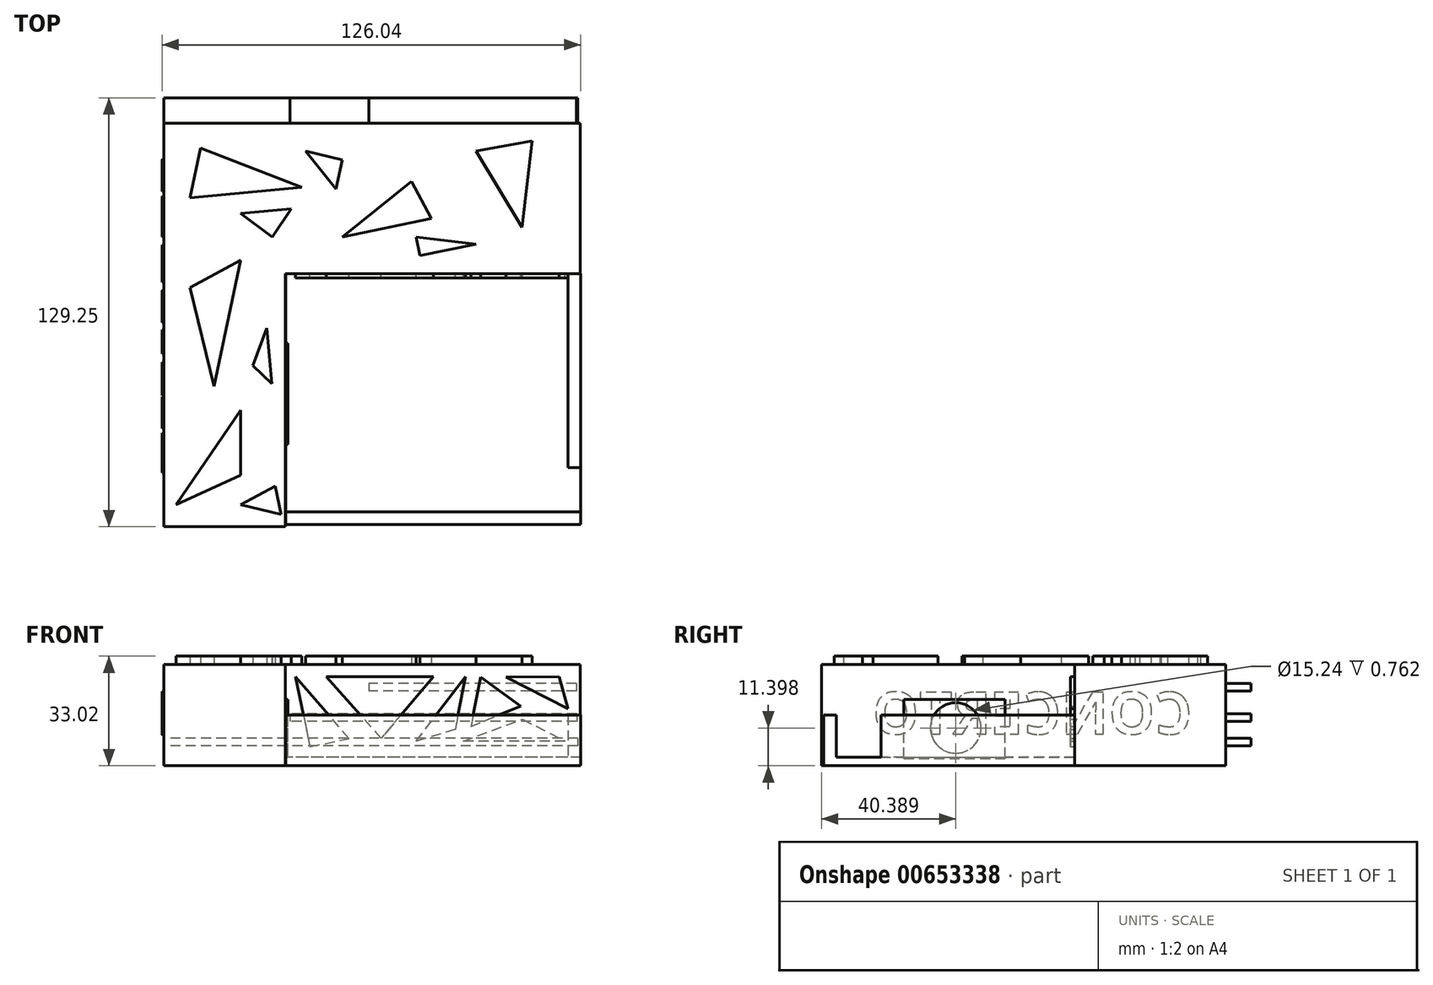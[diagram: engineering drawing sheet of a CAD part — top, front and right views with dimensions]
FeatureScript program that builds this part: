
annotation { "Feature Type Name" : "Feature", "Feature Type Description" : "" }
export const myFeature = defineFeature(function(context is Context, id is Id, definition is map)
    precondition{}
    {
        {
            var Q0;
            Q0=qCreatedBy(makeId("Top.planeOp"),FACE);
            var sketch = newSketch(context, id + "F0", { "sketchPlane" : qUnion([Q0])});
            skLineSegment(sketch, "E0.bottom", {"start": v(-61.74, 45.43) * mm, "end": v(63.6, 45.43) * mm});
            skLineSegment(sketch, "E0.top", {"start": v(-61.74, 0) * mm, "end": v(63.6, 0) * mm});
            skLineSegment(sketch, "E0.left", {"start": v(-61.74, 45.43) * mm, "end": v(-61.74, 0) * mm});
            skLineSegment(sketch, "E0.right", {"start": v(63.6, 45.43) * mm, "end": v(63.6, 0) * mm});
            skSolve(sketch);
        }
        {
            var Q0;
            Q0 = qSketchRegion(id + "F0", true);
            var Q1;
            Q1=makeQuery(id+"F0.imprint","IMPRINT",FACE,{"disambiguationData":[TD([[makeQuery(id+"F0.imprint","IMPRINT",EDGE,{"derivedFrom":sQuery(id+"F0.wireOp",EDGE,"E0.bottom")}),-1.0]])]});
            extrude(context, id + "F1", {"entities" : qUnion([Q0, Q1]), "depth" : 30.48 * mm, "offsetDistance" : 25.4 * mm});
        }
        {
            var Q0;
            Q0=makeQuery(id+"F1.opExtrude","SWEPT_FACE",FACE,{"disambiguationData":[OSD([sQuery(id+"F0.wireOp",EDGE,"E0.top")])]});
            var sketch = newSketch(context, id + "F2", { "sketchPlane" : qUnion([Q0])});
            skLineSegment(sketch, "E1.bottom", {"start": v(-61.74, 30.48) * mm, "end": v(-25.2, 30.48) * mm});
            skLineSegment(sketch, "E1.top", {"start": v(-61.74, 0) * mm, "end": v(-25.2, 0) * mm});
            skLineSegment(sketch, "E1.left", {"start": v(-61.74, 30.48) * mm, "end": v(-61.74, 0) * mm});
            skLineSegment(sketch, "E1.right", {"start": v(-25.2, 30.48) * mm, "end": v(-25.2, 0) * mm});
            skSolve(sketch);
        }
        {
            var Q0;
            Q0=makeQuery(id+"F2.imprint","IMPRINT",FACE,{"disambiguationData":[TD([[makeQuery(id+"F2.imprint","IMPRINT",EDGE,{"derivedFrom":sQuery(id+"F2.wireOp",EDGE,"E1.bottom")}),-1.0]])]});
            extrude(context, id + "F3", {"entities" : qUnion([Q0]), "operationType" : NewBodyOperationType.ADD, "depth" : 76.2 * mm, "offsetDistance" : 25.4 * mm});
        }
        {
            var Q0;
            Q0=qCreatedBy(makeId("Top.planeOp"),FACE);
            var sketch = newSketch(context, id + "F4", { "sketchPlane" : qUnion([Q0])});
            skLineSegment(sketch, "E2.bottom", {"start": v(63.8, 0) * mm, "end": v(-24.98, 0) * mm});
            skLineSegment(sketch, "E2.top", {"start": v(63.8, -75.57) * mm, "end": v(-24.98, -75.57) * mm});
            skLineSegment(sketch, "E2.left", {"start": v(63.8, 0) * mm, "end": v(63.8, -75.57) * mm});
            skLineSegment(sketch, "E2.right", {"start": v(-24.98, 0) * mm, "end": v(-24.98, -75.57) * mm});
            skSolve(sketch);
        }
        {
            var Q0;
            Q0=makeQuery(id+"F4.imprint","IMPRINT",FACE,{"disambiguationData":[TD([[makeQuery(id+"F4.imprint","IMPRINT",EDGE,{"derivedFrom":sQuery(id+"F4.wireOp",EDGE,"E2.bottom")}),1.0]])]});
            extrude(context, id + "F5", {"entities" : qUnion([Q0]), "operationType" : NewBodyOperationType.ADD, "depth" : 2.54 * mm, "offsetDistance" : 25.4 * mm});
        }
        {
            var Q0;
            Q0=makeQuery(id+"F3.boolean.opBoolean","MERGE",FACE,{"derivedFrom":[makeQuery(id+"F1.opExtrude","CAP_FACE",FACE,{"disambiguationData":[OSD([sQuery(id+"F0.wireOp",EDGE,"E0.bottom"),sQuery(id+"F0.wireOp",EDGE,"E0.top"),sQuery(id+"F0.wireOp",EDGE,"E0.left"),sQuery(id+"F0.wireOp",EDGE,"E0.right")])],"isStart":false}),makeQuery(id+"F3.opExtrude","SWEPT_FACE",FACE,{"disambiguationData":[OSD([sQuery(id+"F2.wireOp",EDGE,"E1.bottom")])]})]});
            var sketch = newSketch(context, id + "F6", { "sketchPlane" : qUnion([Q0])});
            skLineSegment(sketch, "E3", {"start": v(-58.02, -69.58) * mm, "end": v(-38.61, -41.09) * mm});
            skLineSegment(sketch, "E4", {"start": v(-38.61, -41.09) * mm, "end": v(-38.61, -60.7) * mm});
            skLineSegment(sketch, "E5", {"start": v(-38.61, -60.7) * mm, "end": v(-58.02, -69.58) * mm});
            skLineSegment(sketch, "E6", {"start": v(-53.9, -4.13) * mm, "end": v(-38.61, 4.13) * mm});
            skLineSegment(sketch, "E7", {"start": v(-38.61, 4.13) * mm, "end": v(-46.66, -33.86) * mm});
            skLineSegment(sketch, "E8", {"start": v(-46.66, -33.86) * mm, "end": v(-53.9, -4.13) * mm});
            skLineSegment(sketch, "E9", {"start": v(-53.9, 22.92) * mm, "end": v(-50.72, 37.86) * mm});
            skLineSegment(sketch, "E10", {"start": v(-50.72, 37.86) * mm, "end": v(-20.23, 26.02) * mm});
            skLineSegment(sketch, "E11", {"start": v(-20.23, 26.02) * mm, "end": v(-53.9, 22.92) * mm});
            skLineSegment(sketch, "E12", {"start": v(-8.05, 11.15) * mm, "end": v(12.8, 27.87) * mm});
            skLineSegment(sketch, "E13", {"start": v(12.8, 27.87) * mm, "end": v(18.85, 16.68) * mm});
            skLineSegment(sketch, "E14", {"start": v(18.85, 16.68) * mm, "end": v(-8.05, 11.15) * mm});
            skLineSegment(sketch, "E15", {"start": v(32.21, 36.96) * mm, "end": v(49.14, 40.06) * mm});
            skLineSegment(sketch, "E16", {"start": v(49.14, 40.06) * mm, "end": v(46.04, 14.04) * mm});
            skLineSegment(sketch, "E17", {"start": v(46.04, 14.04) * mm, "end": v(32.21, 36.96) * mm});
            skLineSegment(sketch, "E18", {"start": v(-38.61, 18.17) * mm, "end": v(-23.4, 19.57) * mm});
            skLineSegment(sketch, "E19", {"start": v(-23.4, 19.57) * mm, "end": v(-29.14, 11.15) * mm});
            skLineSegment(sketch, "E20", {"start": v(-29.14, 11.15) * mm, "end": v(-38.61, 18.17) * mm});
            skLineSegment(sketch, "E21", {"start": v(-34.9, -27.67) * mm, "end": v(-30.77, -16.31) * mm});
            skLineSegment(sketch, "E22", {"start": v(-30.77, -16.31) * mm, "end": v(-29.22, -33.12) * mm});
            skLineSegment(sketch, "E23", {"start": v(-29.22, -33.12) * mm, "end": v(-34.9, -27.67) * mm});
            skLineSegment(sketch, "E24", {"start": v(14.25, 11.15) * mm, "end": v(15.42, 5.45) * mm});
            skLineSegment(sketch, "E25", {"start": v(15.42, 5.45) * mm, "end": v(32.21, 8.9) * mm});
            skLineSegment(sketch, "E26", {"start": v(32.21, 8.9) * mm, "end": v(14.25, 11.15) * mm});
            skLineSegment(sketch, "E27", {"start": v(-19, 36.96) * mm, "end": v(-9.9, 25.61) * mm});
            skLineSegment(sketch, "E28", {"start": v(-9.9, 25.61) * mm, "end": v(-8.05, 34.32) * mm});
            skLineSegment(sketch, "E29", {"start": v(-8.05, 34.32) * mm, "end": v(-19, 36.96) * mm});
            skLineSegment(sketch, "E30", {"start": v(-38.61, -69.58) * mm, "end": v(-28.2, -63.95) * mm});
            skLineSegment(sketch, "E31", {"start": v(-28.2, -63.95) * mm, "end": v(-26.45, -72.43) * mm});
            skLineSegment(sketch, "E32", {"start": v(-26.45, -72.43) * mm, "end": v(-38.61, -69.58) * mm});
            skSolve(sketch);
        }
        {
            var Q0;
            Q0=makeQuery(id+"F6.imprint","IMPRINT",FACE,{"disambiguationData":[TD([[makeQuery(id+"F6.imprint","IMPRINT",EDGE,{"derivedFrom":sQuery(id+"F6.wireOp",EDGE,"E9")}),-1.0]])]});
            var Q1;
            Q1=makeQuery(id+"F6.imprint","IMPRINT",FACE,{"disambiguationData":[TD([[makeQuery(id+"F6.imprint","IMPRINT",EDGE,{"derivedFrom":sQuery(id+"F6.wireOp",EDGE,"E18")}),-1.0]])]});
            var Q2;
            Q2=makeQuery(id+"F6.imprint","IMPRINT",FACE,{"disambiguationData":[TD([[makeQuery(id+"F6.imprint","IMPRINT",EDGE,{"derivedFrom":sQuery(id+"F6.wireOp",EDGE,"E6")}),-1.0]])]});
            var Q3;
            Q3=makeQuery(id+"F6.imprint","IMPRINT",FACE,{"disambiguationData":[TD([[makeQuery(id+"F6.imprint","IMPRINT",EDGE,{"derivedFrom":sQuery(id+"F6.wireOp",EDGE,"E21")}),-1.0]])]});
            var Q4;
            Q4=makeQuery(id+"F6.imprint","IMPRINT",FACE,{"disambiguationData":[TD([[makeQuery(id+"F6.imprint","IMPRINT",EDGE,{"derivedFrom":sQuery(id+"F6.wireOp",EDGE,"E3")}),-1.0]])]});
            var Q5;
            Q5=makeQuery(id+"F6.imprint","IMPRINT",FACE,{"disambiguationData":[TD([[makeQuery(id+"F6.imprint","IMPRINT",EDGE,{"derivedFrom":sQuery(id+"F6.wireOp",EDGE,"E30")}),-1.0]])]});
            var Q6;
            Q6=makeQuery(id+"F6.imprint","IMPRINT",FACE,{"disambiguationData":[TD([[makeQuery(id+"F6.imprint","IMPRINT",EDGE,{"derivedFrom":sQuery(id+"F6.wireOp",EDGE,"E27")}),1.0]])]});
            var Q7;
            Q7=makeQuery(id+"F6.imprint","IMPRINT",FACE,{"disambiguationData":[TD([[makeQuery(id+"F6.imprint","IMPRINT",EDGE,{"derivedFrom":sQuery(id+"F6.wireOp",EDGE,"E12")}),-1.0]])]});
            var Q8;
            Q8=makeQuery(id+"F6.imprint","IMPRINT",FACE,{"disambiguationData":[TD([[makeQuery(id+"F6.imprint","IMPRINT",EDGE,{"derivedFrom":sQuery(id+"F6.wireOp",EDGE,"E24")}),1.0]])]});
            var Q9;
            Q9=makeQuery(id+"F6.imprint","IMPRINT",FACE,{"disambiguationData":[TD([[makeQuery(id+"F6.imprint","IMPRINT",EDGE,{"derivedFrom":sQuery(id+"F6.wireOp",EDGE,"E15")}),-1.0]])]});
            extrude(context, id + "F7", {"entities" : qUnion([Q0, Q1, Q2, Q3, Q4, Q5, Q6, Q7, Q8, Q9]), "operationType" : NewBodyOperationType.ADD, "depth" : 2.54 * mm, "offsetDistance" : 25.4 * mm});
        }
        {
            var Q0;
            Q0=makeQuery(id+"F1.opExtrude","SWEPT_FACE",FACE,{"disambiguationData":[OSD([sQuery(id+"F0.wireOp",EDGE,"E0.top")])]});
            var sketch = newSketch(context, id + "F8", { "sketchPlane" : qUnion([Q0])});
            skLineSegment(sketch, "E33", {"start": v(-22.1, 26.84) * mm, "end": v(-17.76, 5.78) * mm});
            skLineSegment(sketch, "E34", {"start": v(-17.76, 5.78) * mm, "end": v(-6.02, 8.2) * mm});
            skLineSegment(sketch, "E35", {"start": v(-6.02, 8.2) * mm, "end": v(-22.1, 26.84) * mm});
            skLineSegment(sketch, "E36", {"start": v(-12.8, 26.84) * mm, "end": v(19.4, 26.84) * mm});
            skLineSegment(sketch, "E37", {"start": v(19.4, 26.84) * mm, "end": v(3.72, 8.26) * mm});
            skLineSegment(sketch, "E38", {"start": v(3.72, 8.26) * mm, "end": v(-12.8, 26.84) * mm});
            skLineSegment(sketch, "E39", {"start": v(14.25, 7.43) * mm, "end": v(29.11, 26.84) * mm});
            skLineSegment(sketch, "E40", {"start": v(29.11, 26.84) * mm, "end": v(26.02, 10.94) * mm});
            skLineSegment(sketch, "E41", {"start": v(26.02, 10.94) * mm, "end": v(14.25, 7.43) * mm});
            skLineSegment(sketch, "E42", {"start": v(28.5, 7.43) * mm, "end": v(46.25, 14.04) * mm});
            skLineSegment(sketch, "E43", {"start": v(46.25, 14.04) * mm, "end": v(59.05, 7.43) * mm});
            skLineSegment(sketch, "E44", {"start": v(59.05, 7.43) * mm, "end": v(28.5, 7.43) * mm});
            skLineSegment(sketch, "E45", {"start": v(31.38, 14.25) * mm, "end": v(33.66, 26.84) * mm});
            skSolve(sketch);
        }
        {
            var Q0;
            Q0=makeQuery(id+"F8.imprint","IMPRINT",FACE,{"disambiguationData":[TD([[makeQuery(id+"F8.imprint","IMPRINT",EDGE,{"derivedFrom":sQuery(id+"F8.wireOp",EDGE,"E33")}),1.0]])]});
            var Q1;
            Q1=makeQuery(id+"F8.imprint","IMPRINT",FACE,{"disambiguationData":[TD([[makeQuery(id+"F8.imprint","IMPRINT",EDGE,{"derivedFrom":sQuery(id+"F8.wireOp",EDGE,"E36")}),-1.0]])]});
            var Q2;
            Q2=makeQuery(id+"F8.imprint","IMPRINT",FACE,{"disambiguationData":[TD([[makeQuery(id+"F8.imprint","IMPRINT",EDGE,{"derivedFrom":sQuery(id+"F8.wireOp",EDGE,"E39")}),-1.0]])]});
            var Q3;
            Q3=makeQuery(id+"F8.imprint","IMPRINT",FACE,{"disambiguationData":[TD([[makeQuery(id+"F8.imprint","IMPRINT",EDGE,{"derivedFrom":sQuery(id+"F8.wireOp",EDGE,"E42")}),-1.0]])]});
            extrude(context, id + "F9", {"entities" : qUnion([Q0, Q1, Q2, Q3]), "operationType" : NewBodyOperationType.ADD, "depth" : 1.27 * mm, "offsetDistance" : 25.4 * mm});
        }
        {
            var Q0;
            Q0=makeQuery(id+"F1.opExtrude","SWEPT_FACE",FACE,{"disambiguationData":[OSD([sQuery(id+"F0.wireOp",EDGE,"E0.top")])]});
            var sketch = newSketch(context, id + "F10", { "sketchPlane" : qUnion([Q0])});
            skLineSegment(sketch, "E46", {"start": v(33.62, 26.67) * mm, "end": v(30.74, 11.88) * mm});
            skLineSegment(sketch, "E47", {"start": v(30.74, 11.88) * mm, "end": v(45.78, 17.98) * mm});
            skLineSegment(sketch, "E48", {"start": v(45.78, 17.98) * mm, "end": v(33.62, 26.67) * mm});
            skLineSegment(sketch, "E49", {"start": v(41.34, 26.67) * mm, "end": v(59.95, 17.25) * mm});
            skLineSegment(sketch, "E50", {"start": v(59.95, 17.25) * mm, "end": v(57.33, 26.84) * mm});
            skLineSegment(sketch, "E51", {"start": v(57.33, 26.84) * mm, "end": v(41.34, 26.67) * mm});
            skSolve(sketch);
        }
        {
            var Q0;
            Q0=makeQuery(id+"F10.imprint","IMPRINT",FACE,{"disambiguationData":[TD([[makeQuery(id+"F10.imprint","IMPRINT",EDGE,{"derivedFrom":sQuery(id+"F10.wireOp",EDGE,"E46")}),1.0]])]});
            var Q1;
            Q1=makeQuery(id+"F10.imprint","IMPRINT",FACE,{"disambiguationData":[TD([[makeQuery(id+"F10.imprint","IMPRINT",EDGE,{"derivedFrom":sQuery(id+"F10.wireOp",EDGE,"E49")}),1.0]])]});
            extrude(context, id + "F11", {"entities" : qUnion([Q0, Q1]), "operationType" : NewBodyOperationType.ADD, "depth" : 1.27 * mm, "offsetDistance" : 25.4 * mm});
        }
        {
            var Q0;
            Q0=makeQuery(id+"F5.opExtrude","CAP_FACE",FACE,{"disambiguationData":[OSD([sQuery(id+"F4.wireOp",EDGE,"E2.bottom"),sQuery(id+"F4.wireOp",EDGE,"E2.top"),sQuery(id+"F4.wireOp",EDGE,"E2.left"),sQuery(id+"F4.wireOp",EDGE,"E2.right")])],"isStart":false});
            var sketch = newSketch(context, id + "F12", { "sketchPlane" : qUnion([Q0])});
            skLineSegment(sketch, "E52.bottom", {"start": v(63.8, -71.76) * mm, "end": v(-24.98, -71.76) * mm});
            skLineSegment(sketch, "E52.top", {"start": v(63.8, -75.57) * mm, "end": v(-24.98, -75.57) * mm});
            skLineSegment(sketch, "E52.left", {"start": v(63.8, -71.76) * mm, "end": v(63.8, -75.57) * mm});
            skLineSegment(sketch, "E52.right", {"start": v(-24.98, -71.76) * mm, "end": v(-24.98, -75.57) * mm});
            skLineSegment(sketch, "E53.bottom", {"start": v(63.8, -58.34) * mm, "end": v(60, -58.34) * mm});
            skLineSegment(sketch, "E53.top", {"start": v(63.8, 0) * mm, "end": v(60, 0) * mm});
            skLineSegment(sketch, "E53.left", {"start": v(63.8, -58.34) * mm, "end": v(63.8, 0) * mm});
            skLineSegment(sketch, "E53.right", {"start": v(60, -58.34) * mm, "end": v(60, 0) * mm});
            skSolve(sketch);
        }
        {
            var Q0;
            Q0=makeQuery(id+"F12.imprint","IMPRINT",FACE,{"disambiguationData":[TD([[makeQuery(id+"F12.imprint","IMPRINT",EDGE,{"derivedFrom":sQuery(id+"F12.wireOp",EDGE,"E52.bottom")}),1.0]])]});
            var Q1;
            Q1=makeQuery(id+"F12.imprint","IMPRINT",FACE,{"disambiguationData":[TD([[makeQuery(id+"F12.imprint","IMPRINT",EDGE,{"derivedFrom":sQuery(id+"F12.wireOp",EDGE,"E53.bottom")}),-1.0]])]});
            extrude(context, id + "F13", {"entities" : qUnion([Q0, Q1]), "operationType" : NewBodyOperationType.ADD, "depth" : 12.7 * mm, "offsetDistance" : 25.4 * mm});
        }
        {
            var Q0;
            Q0=makeQuery(id+"F3.opExtrude","SWEPT_FACE",FACE,{"disambiguationData":[OSD([sQuery(id+"F2.wireOp",EDGE,"E1.right")])]});
            var sketch = newSketch(context, id + "F14", { "sketchPlane" : qUnion([Q0])});
            skLineSegment(sketch, "E54.bottom", {"start": v(-51.45, 2.25) * mm, "end": v(-20.97, 2.25) * mm});
            skLineSegment(sketch, "E54.top", {"start": v(-51.45, 20.03) * mm, "end": v(-20.97, 20.03) * mm});
            skLineSegment(sketch, "E54.left", {"start": v(-51.45, 2.25) * mm, "end": v(-51.45, 20.03) * mm});
            skLineSegment(sketch, "E54.right", {"start": v(-20.97, 2.25) * mm, "end": v(-20.97, 20.03) * mm});
            skSolve(sketch);
        }
        {
            var Q0;
            Q0=makeQuery(id+"F14.imprint","IMPRINT",FACE,{"disambiguationData":[TD([[makeQuery(id+"F14.imprint","IMPRINT",EDGE,{"derivedFrom":sQuery(id+"F14.wireOp",EDGE,"E54.bottom")}),1.0]])]});
            extrude(context, id + "F15", {"entities" : qUnion([Q0]), "operationType" : NewBodyOperationType.ADD, "depth" : 0.76 * mm, "offsetDistance" : 25.4 * mm});
        }
        {
            var Q0;
            Q0=makeQuery(id+"F15.opExtrude","CAP_FACE",FACE,{"disambiguationData":[OSD([sQuery(id+"F14.wireOp",EDGE,"E54.bottom"),sQuery(id+"F14.wireOp",EDGE,"E54.top"),sQuery(id+"F14.wireOp",EDGE,"E54.left"),sQuery(id+"F14.wireOp",EDGE,"E54.right")])],"isStart":false});
            var sketch = newSketch(context, id + "F16", { "sketchPlane" : qUnion([Q0])});
            skCircle(sketch, "E55", {"center": v(-35.81, 11.4) * mm, "radius": 7.62 * mm});
            skSolve(sketch);
        }
        {
            var Q0;
            Q0=makeQuery(id+"F16.imprint","IMPRINT",FACE,{"disambiguationData":[TD([[makeQuery(id+"F16.imprint","IMPRINT",EDGE,{"derivedFrom":sQuery(id+"F16.wireOp",EDGE,"E55")}),1.0]])]});
            extrude(context, id + "F17", {"entities" : qUnion([Q0]), "operationType" : NewBodyOperationType.REMOVE, "oppositeDirection" : true, "depth" : 0.76 * mm, "offsetDistance" : 25.4 * mm});
        }
        {
            var Q0;
            Q0=makeQuery(id+"F1.opExtrude","SWEPT_FACE",FACE,{"disambiguationData":[OSD([sQuery(id+"F0.wireOp",EDGE,"E0.bottom")])]});
            var sketch = newSketch(context, id + "F18", { "sketchPlane" : qUnion([Q0])});
            skLineSegment(sketch, "E56.bottom", {"start": v(-62.87, 8.26) * mm, "end": v(64.13, 8.26) * mm});
            skLineSegment(sketch, "E56.top", {"start": v(-62.87, 5.97) * mm, "end": v(64.13, 5.97) * mm});
            skLineSegment(sketch, "E56.left", {"start": v(-62.87, 8.26) * mm, "end": v(-62.87, 5.97) * mm});
            skLineSegment(sketch, "E56.right", {"start": v(64.13, 8.26) * mm, "end": v(64.13, 5.97) * mm});
            skLineSegment(sketch, "E57.bottom", {"start": v(-62.61, 15.62) * mm, "end": v(23.75, 15.62) * mm});
            skLineSegment(sketch, "E57.top", {"start": v(-62.61, 13.34) * mm, "end": v(23.75, 13.34) * mm});
            skLineSegment(sketch, "E57.left", {"start": v(-62.61, 15.62) * mm, "end": v(-62.61, 13.34) * mm});
            skLineSegment(sketch, "E57.right", {"start": v(23.75, 15.62) * mm, "end": v(23.75, 13.34) * mm});
            skLineSegment(sketch, "E58.bottom", {"start": v(-62.48, 24.77) * mm, "end": v(0, 24.77) * mm});
            skLineSegment(sketch, "E58.top", {"start": v(-62.48, 22.48) * mm, "end": v(0, 22.48) * mm});
            skLineSegment(sketch, "E58.left", {"start": v(-62.48, 24.77) * mm, "end": v(-62.48, 22.48) * mm});
            skLineSegment(sketch, "E58.right", {"start": v(0, 24.77) * mm, "end": v(0, 22.48) * mm});
            skSolve(sketch);
        }
        {
            var Q0;
            Q0=makeQuery(id+"F18.imprint","IMPRINT",FACE,{"disambiguationData":[TD([[makeQuery(id+"F18.imprint","IMPRINT",EDGE,{"derivedFrom":sQuery(id+"F18.wireOp",EDGE,"E58.bottom")}),-1.0]])]});
            var Q1;
            Q1=makeQuery(id+"F18.imprint","IMPRINT",FACE,{"disambiguationData":[TD([[makeQuery(id+"F18.imprint","IMPRINT",EDGE,{"derivedFrom":sQuery(id+"F18.wireOp",EDGE,"E57.bottom")}),-1.0]])]});
            var Q2;
            {var subQ0=sQuery(id+"F18.wireOp",EDGE,"E56.left");Q2=makeQuery(id+"F18.imprint","IMPRINT",FACE,{"disambiguationData":[TD([[makeQuery(id+"F18.imprint","IMPRINT",EDGE,{"derivedFrom":subQ0}),1.0]])]});}
            extrude(context, id + "F19", {"entities" : qUnion([Q0, Q1, Q2]), "operationType" : NewBodyOperationType.ADD, "depth" : 7.62 * mm, "offsetDistance" : 25.4 * mm});
        }
        {
            var Q0;
            {var subQ0=sQuery(id+"F0.wireOp",EDGE,"E0.left");Q0=makeQuery(id+"F19.boolean.opBoolean","MERGE",FACE,{"derivedFrom":[makeQuery(id+"F3.boolean.opBoolean","MERGE",FACE,{"derivedFrom":[makeQuery(id+"F1.opExtrude","SWEPT_FACE",FACE,{"disambiguationData":[OSD([subQ0])]}),makeQuery(id+"F3.opExtrude","SWEPT_FACE",FACE,{"disambiguationData":[OSD([sQuery(id+"F2.wireOp",EDGE,"E1.left")])]})]}),makeQuery(id+"F19.opExtrude","SWEPT_FACE",FACE,{"disambiguationData":[OSD([sQuery(id+"F0.wireOp",EDGE,"E0.bottom"),subQ0])]})]});}
            var sketch = newSketch(context, id + "F20", { "sketchPlane" : qUnion([Q0])});
            skText(sketch, "E59", { "text": "CONCERTO", "fontName": "OpenSans-Bold.ttf"});
            const initialGuessF20  = {"E59": [-0.03538, 0.0096, 1, 0, 0.01265]};
            skSetInitialGuess(sketch, initialGuessF20);
            skSolve(sketch);
        }
        {
            var Q0;
            Q0 = qSketchRegion(id + "F20", true);
            extrude(context, id + "F21", {"entities" : qUnion([Q0]), "operationType" : NewBodyOperationType.ADD, "depth" : 0.5 * mm, "offsetDistance" : 25.4 * mm});
        }
    });
